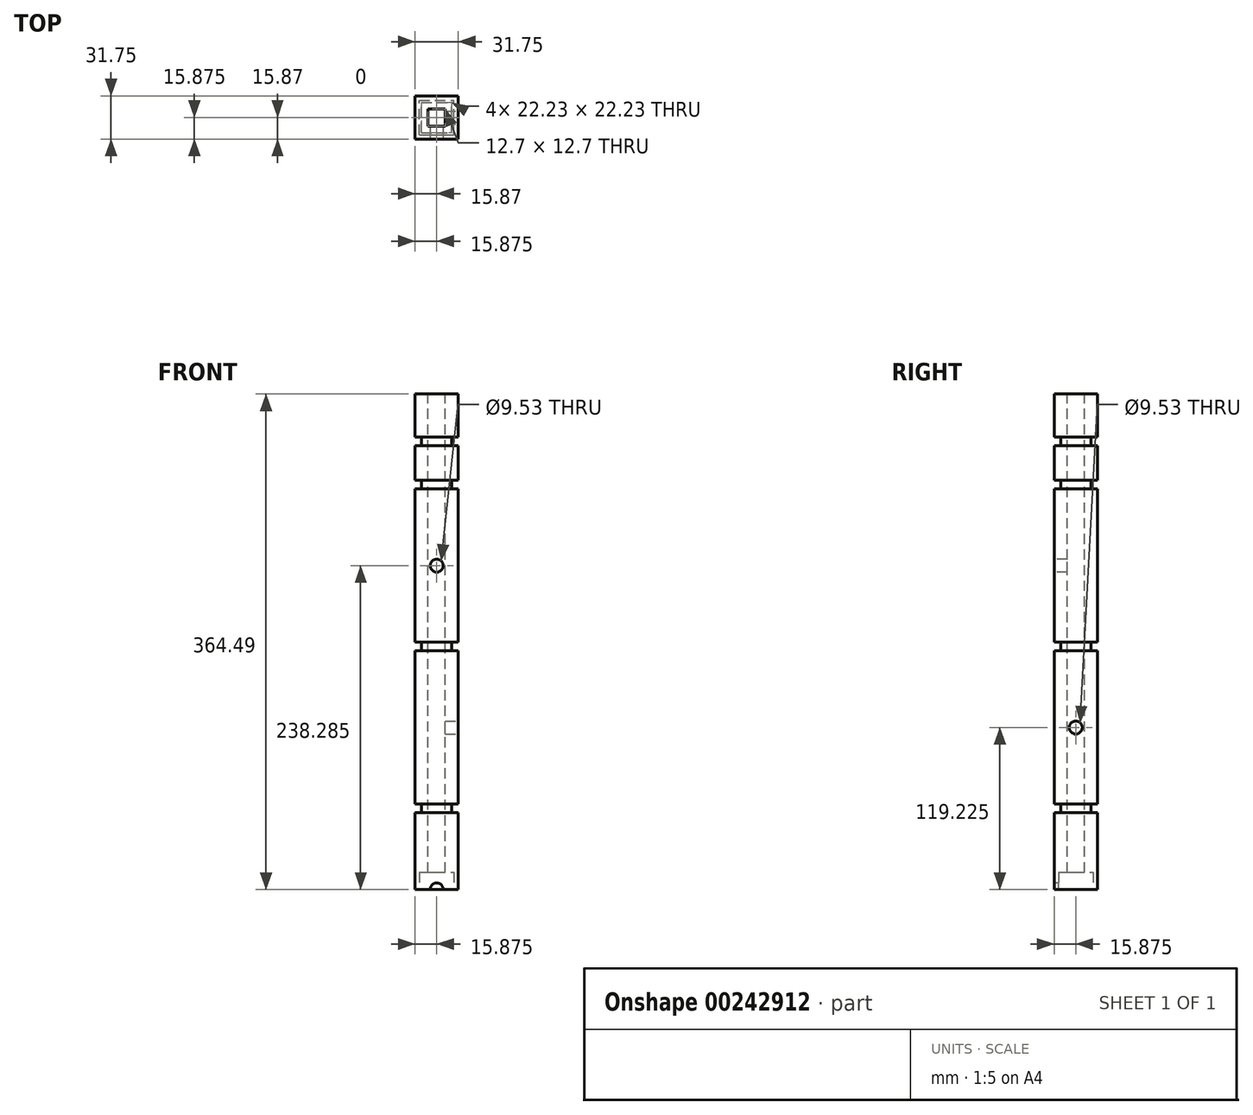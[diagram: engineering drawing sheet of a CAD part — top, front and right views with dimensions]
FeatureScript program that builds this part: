
annotation { "Feature Type Name" : "Feature", "Feature Type Description" : "" }
export const myFeature = defineFeature(function(context is Context, id is Id, definition is map)
    precondition{}
    {
        {
            var Q0;
            Q0=qCreatedBy(makeId("Top.planeOp"),FACE);
            var sketch = newSketch(context, id + "F0", { "sketchPlane" : qUnion([Q0])});
            skLineSegment(sketch, "E0", {"start": v(0, 0) * mm, "end": v(0, 31.75) * mm});
            skLineSegment(sketch, "E1", {"start": v(0, 31.75) * mm, "end": v(31.75, 31.75) * mm});
            skLineSegment(sketch, "E2", {"start": v(31.75, 31.75) * mm, "end": v(31.75, 0) * mm});
            skLineSegment(sketch, "E3", {"start": v(31.75, 0) * mm, "end": v(0, 0) * mm});
            skSolve(sketch);
        }
        {
            var Q0;
            Q0=makeQuery(id+"F0.imprint","IMPRINT",FACE,{"disambiguationData":[TD([[makeQuery(id+"F0.imprint","IMPRINT",EDGE,{"derivedFrom":sQuery(id+"F0.wireOp",EDGE,"E0")}),-1.0]])]});
            extrude(context, id + "F1", {"entities" : qUnion([Q0]), "depth" : 60.33 * mm});
        }
        {
            var Q0;
            Q0=makeQuery(id+"F1.opExtrude","CAP_FACE",FACE,{"disambiguationData":[OSD([sQuery(id+"F0.wireOp",EDGE,"E0"),sQuery(id+"F0.wireOp",EDGE,"E1"),sQuery(id+"F0.wireOp",EDGE,"E2"),sQuery(id+"F0.wireOp",EDGE,"E3")])],"isStart":false});
            var sketch = newSketch(context, id + "F2", { "sketchPlane" : qUnion([Q0])});
            skLineSegment(sketch, "E4", {"start": v(4.76, 4.76) * mm, "end": v(4.76, 26.99) * mm});
            skLineSegment(sketch, "E5", {"start": v(4.76, 26.99) * mm, "end": v(26.99, 26.99) * mm});
            skLineSegment(sketch, "E6", {"start": v(26.99, 26.99) * mm, "end": v(26.99, 4.76) * mm});
            skLineSegment(sketch, "E7", {"start": v(26.99, 4.76) * mm, "end": v(4.76, 4.76) * mm});
            skSolve(sketch);
        }
        {
            var Q0;
            Q0=makeQuery(id+"F2.imprint","IMPRINT",FACE,{"disambiguationData":[TD([[makeQuery(id+"F2.imprint","IMPRINT",EDGE,{"derivedFrom":sQuery(id+"F2.wireOp",EDGE,"E4")}),-1.0]])]});
            extrude(context, id + "F3", {"entities" : qUnion([Q0]), "operationType" : NewBodyOperationType.ADD, "depth" : 6.35 * mm});
        }
        {
            var Q0;
            Q0=makeQuery(id+"F3.opExtrude","CAP_FACE",FACE,{"disambiguationData":[OSD([sQuery(id+"F2.wireOp",EDGE,"E4"),sQuery(id+"F2.wireOp",EDGE,"E5"),sQuery(id+"F2.wireOp",EDGE,"E6"),sQuery(id+"F2.wireOp",EDGE,"E7")])],"isStart":false});
            var sketch = newSketch(context, id + "F4", { "sketchPlane" : qUnion([Q0])});
            skLineSegment(sketch, "E8.bottom", {"start": v(0, 0) * mm, "end": v(31.75, 0) * mm});
            skLineSegment(sketch, "E8.top", {"start": v(0, 31.75) * mm, "end": v(31.75, 31.75) * mm});
            skLineSegment(sketch, "E8.left", {"start": v(0, 0) * mm, "end": v(0, 31.75) * mm});
            skLineSegment(sketch, "E8.right", {"start": v(31.75, 0) * mm, "end": v(31.75, 31.75) * mm});
            skSolve(sketch);
        }
        {
            var Q0;
            Q0=qSketchRegion(id+"F4",true);
            extrude(context, id + "F5", {"entities" : qUnion([Q0]), "operationType" : NewBodyOperationType.ADD, "depth" : 112.7 * mm});
        }
        {
            var Q0;
            Q0=makeQuery(id+"F5.opExtrude","CAP_FACE",FACE,{"disambiguationData":[OSD([sQuery(id+"F4.wireOp",EDGE,"E8.bottom"),sQuery(id+"F4.wireOp",EDGE,"E8.top"),sQuery(id+"F4.wireOp",EDGE,"E8.left"),sQuery(id+"F4.wireOp",EDGE,"E8.right")])],"isStart":false});
            var sketch = newSketch(context, id + "F6", { "sketchPlane" : qUnion([Q0])});
            skLineSegment(sketch, "E9.bottom", {"start": v(0, 0) * mm, "end": v(4.76, 0) * mm});
            skLineSegment(sketch, "E9.top", {"start": v(0, 4.76) * mm, "end": v(4.76, 4.76) * mm});
            skLineSegment(sketch, "E9.left", {"start": v(0, 0) * mm, "end": v(0, 4.76) * mm});
            skLineSegment(sketch, "E9.right", {"start": v(4.76, 0) * mm, "end": v(4.76, 4.76) * mm});
            skLineSegment(sketch, "E10.bottom", {"start": v(4.76, 4.76) * mm, "end": v(26.99, 4.76) * mm});
            skLineSegment(sketch, "E10.top", {"start": v(4.76, 26.99) * mm, "end": v(26.99, 26.99) * mm});
            skLineSegment(sketch, "E10.left", {"start": v(4.76, 4.76) * mm, "end": v(4.76, 26.99) * mm});
            skLineSegment(sketch, "E10.right", {"start": v(26.99, 4.76) * mm, "end": v(26.99, 26.99) * mm});
            skSolve(sketch);
        }
        {
            var Q0;
            Q0=makeQuery(id+"F6.imprint","IMPRINT",FACE,{"disambiguationData":[TD([[makeQuery(id+"F6.imprint","IMPRINT",EDGE,{"derivedFrom":sQuery(id+"F6.wireOp",EDGE,"E10.bottom")}),1.0]])]});
            extrude(context, id + "F7", {"entities" : qUnion([Q0]), "operationType" : NewBodyOperationType.ADD, "depth" : 6.35 * mm});
        }
        {
            var Q0;
            Q0=makeQuery(id+"F7.opExtrude","CAP_FACE",FACE,{"disambiguationData":[OSD([sQuery(id+"F6.wireOp",EDGE,"E10.bottom"),sQuery(id+"F6.wireOp",EDGE,"E10.top"),sQuery(id+"F6.wireOp",EDGE,"E10.left"),sQuery(id+"F6.wireOp",EDGE,"E10.right")])],"isStart":false});
            var sketch = newSketch(context, id + "F8", { "sketchPlane" : qUnion([Q0])});
            skLineSegment(sketch, "E11.bottom", {"start": v(0, 0) * mm, "end": v(31.75, 0) * mm});
            skLineSegment(sketch, "E11.top", {"start": v(0, 31.75) * mm, "end": v(31.75, 31.75) * mm});
            skLineSegment(sketch, "E11.left", {"start": v(0, 0) * mm, "end": v(0, 31.75) * mm});
            skLineSegment(sketch, "E11.right", {"start": v(31.75, 0) * mm, "end": v(31.75, 31.75) * mm});
            skSolve(sketch);
        }
        {
            var Q0;
            Q0=makeQuery(id+"F8.imprint","IMPRINT",FACE,{"disambiguationData":[TD([[makeQuery(id+"F8.imprint","IMPRINT",EDGE,{"derivedFrom":sQuery(id+"F8.wireOp",EDGE,"E11.bottom")}),1.0]])]});
            var Q1;
            Q1=makeQuery(id+"F8.imprint","IMPRINT",FACE,{"disambiguationData":[TD([[makeQuery(id+"F8.imprint","IMPRINT",EDGE,{"derivedFrom":makeQuery(id+"F7.opExtrude","CAP_EDGE",EDGE,{"disambiguationData":[OSD([sQuery(id+"F6.wireOp",EDGE,"E10.bottom")])],"isStart":false})}),1.0]])]});
            extrude(context, id + "F9", {"entities" : qUnion([Q0, Q1]), "operationType" : NewBodyOperationType.ADD, "depth" : 112.7 * mm});
        }
        {
            var Q0;
            Q0=makeQuery(id+"F9.opExtrude","CAP_FACE",FACE,{"disambiguationData":[OSD([sQuery(id+"F8.wireOp",EDGE,"E11.bottom"),sQuery(id+"F8.wireOp",EDGE,"E11.top"),sQuery(id+"F8.wireOp",EDGE,"E11.left"),sQuery(id+"F8.wireOp",EDGE,"E11.right")])],"isStart":false});
            var sketch = newSketch(context, id + "F10", { "sketchPlane" : qUnion([Q0])});
            skLineSegment(sketch, "E12.bottom", {"start": v(0, 0) * mm, "end": v(4.76, 0) * mm});
            skLineSegment(sketch, "E12.top", {"start": v(0, 4.76) * mm, "end": v(4.76, 4.76) * mm});
            skLineSegment(sketch, "E12.left", {"start": v(0, 0) * mm, "end": v(0, 4.76) * mm});
            skLineSegment(sketch, "E12.right", {"start": v(4.76, 0) * mm, "end": v(4.76, 4.76) * mm});
            skLineSegment(sketch, "E13.bottom", {"start": v(4.76, 4.76) * mm, "end": v(27, 4.76) * mm});
            skLineSegment(sketch, "E13.top", {"start": v(4.76, 26.99) * mm, "end": v(26.99, 26.99) * mm});
            skLineSegment(sketch, "E13.left", {"start": v(4.76, 4.76) * mm, "end": v(4.76, 26.99) * mm});
            skLineSegment(sketch, "E13.right", {"start": v(27, 4.76) * mm, "end": v(26.99, 26.99) * mm});
            skLineSegment(sketch, "E14.bottom", {"start": v(26.99, 26.99) * mm, "end": v(31.75, 26.99) * mm});
            skLineSegment(sketch, "E14.top", {"start": v(26.99, 31.75) * mm, "end": v(31.75, 31.75) * mm});
            skLineSegment(sketch, "E14.left", {"start": v(26.99, 26.99) * mm, "end": v(26.99, 31.75) * mm});
            skLineSegment(sketch, "E14.right", {"start": v(31.75, 26.99) * mm, "end": v(31.75, 31.75) * mm});
            skSolve(sketch);
        }
        {
            var Q0;
            Q0=makeQuery(id+"F10.imprint","IMPRINT",FACE,{"disambiguationData":[TD([[makeQuery(id+"F10.imprint","IMPRINT",EDGE,{"derivedFrom":sQuery(id+"F10.wireOp",EDGE,"E13.bottom")}),1.0]])]});
            extrude(context, id + "F11", {"entities" : qUnion([Q0]), "operationType" : NewBodyOperationType.ADD, "depth" : 6.35 * mm});
        }
        {
            var Q0;
            Q0=makeQuery(id+"F11.opExtrude","CAP_FACE",FACE,{"disambiguationData":[OSD([sQuery(id+"F10.wireOp",EDGE,"E13.bottom"),sQuery(id+"F10.wireOp",EDGE,"E13.top"),sQuery(id+"F10.wireOp",EDGE,"E13.left"),sQuery(id+"F10.wireOp",EDGE,"E13.right")])],"isStart":false});
            var sketch = newSketch(context, id + "F12", { "sketchPlane" : qUnion([Q0])});
            skLineSegment(sketch, "E15.bottom", {"start": v(0, 0) * mm, "end": v(31.75, 0) * mm});
            skLineSegment(sketch, "E15.top", {"start": v(0, 31.75) * mm, "end": v(31.75, 31.75) * mm});
            skLineSegment(sketch, "E15.left", {"start": v(0, 0) * mm, "end": v(0, 31.75) * mm});
            skLineSegment(sketch, "E15.right", {"start": v(31.75, 0) * mm, "end": v(31.75, 31.75) * mm});
            skSolve(sketch);
        }
        {
            var Q0;
            Q0=makeQuery(id+"F12.imprint","IMPRINT",FACE,{"disambiguationData":[TD([[makeQuery(id+"F12.imprint","IMPRINT",EDGE,{"derivedFrom":makeQuery(id+"F11.opExtrude","CAP_EDGE",EDGE,{"disambiguationData":[OSD([sQuery(id+"F10.wireOp",EDGE,"E13.bottom")])],"isStart":false})}),1.0]])]});
            var Q1;
            Q1=makeQuery(id+"F12.imprint","IMPRINT",FACE,{"disambiguationData":[TD([[makeQuery(id+"F12.imprint","IMPRINT",EDGE,{"derivedFrom":sQuery(id+"F12.wireOp",EDGE,"E15.bottom")}),1.0]])]});
            extrude(context, id + "F13", {"entities" : qUnion([Q0, Q1]), "operationType" : NewBodyOperationType.ADD, "depth" : 112.7 * mm});
        }
        {
            var Q0;
            Q0=makeQuery(id+"F13.opExtrude","CAP_FACE",FACE,{"disambiguationData":[OSD([sQuery(id+"F12.wireOp",EDGE,"E15.bottom"),sQuery(id+"F12.wireOp",EDGE,"E15.top"),sQuery(id+"F12.wireOp",EDGE,"E15.left"),sQuery(id+"F12.wireOp",EDGE,"E15.right")])],"isStart":false});
            var sketch = newSketch(context, id + "F14", { "sketchPlane" : qUnion([Q0])});
            skLineSegment(sketch, "E16.bottom", {"start": v(0, 0) * mm, "end": v(4.76, 0) * mm});
            skLineSegment(sketch, "E16.top", {"start": v(0, 4.76) * mm, "end": v(4.76, 4.76) * mm});
            skLineSegment(sketch, "E16.left", {"start": v(0, 0) * mm, "end": v(0, 4.76) * mm});
            skLineSegment(sketch, "E16.right", {"start": v(4.76, 0) * mm, "end": v(4.76, 4.76) * mm});
            skLineSegment(sketch, "E17.bottom", {"start": v(4.76, 4.76) * mm, "end": v(27, 4.76) * mm});
            skLineSegment(sketch, "E17.top", {"start": v(4.76, 26.99) * mm, "end": v(26.99, 26.99) * mm});
            skLineSegment(sketch, "E17.left", {"start": v(4.76, 4.76) * mm, "end": v(4.76, 26.99) * mm});
            skLineSegment(sketch, "E17.right", {"start": v(27, 4.76) * mm, "end": v(26.99, 26.99) * mm});
            skLineSegment(sketch, "E18.bottom", {"start": v(26.99, 26.99) * mm, "end": v(31.75, 26.99) * mm});
            skLineSegment(sketch, "E18.top", {"start": v(26.99, 31.75) * mm, "end": v(31.75, 31.75) * mm});
            skLineSegment(sketch, "E18.left", {"start": v(26.99, 26.99) * mm, "end": v(26.99, 31.75) * mm});
            skLineSegment(sketch, "E18.right", {"start": v(31.75, 26.99) * mm, "end": v(31.75, 31.75) * mm});
            skSolve(sketch);
        }
        {
            var Q0;
            Q0=makeQuery(id+"F14.imprint","IMPRINT",FACE,{"disambiguationData":[TD([[makeQuery(id+"F14.imprint","IMPRINT",EDGE,{"derivedFrom":sQuery(id+"F14.wireOp",EDGE,"E17.bottom")}),1.0]])]});
            extrude(context, id + "F15", {"entities" : qUnion([Q0]), "operationType" : NewBodyOperationType.ADD, "depth" : 6.35 * mm});
        }
        {
            var Q0;
            Q0=makeQuery(id+"F15.opExtrude","CAP_FACE",FACE,{"disambiguationData":[OSD([sQuery(id+"F14.wireOp",EDGE,"E17.bottom"),sQuery(id+"F14.wireOp",EDGE,"E17.top"),sQuery(id+"F14.wireOp",EDGE,"E17.left"),sQuery(id+"F14.wireOp",EDGE,"E17.right")])],"isStart":false});
            var sketch = newSketch(context, id + "F16", { "sketchPlane" : qUnion([Q0])});
            skLineSegment(sketch, "E19.bottom", {"start": v(0, 0) * mm, "end": v(31.75, 0) * mm});
            skLineSegment(sketch, "E19.top", {"start": v(0, 31.75) * mm, "end": v(31.75, 31.75) * mm});
            skLineSegment(sketch, "E19.left", {"start": v(0, 0) * mm, "end": v(0, 31.75) * mm});
            skLineSegment(sketch, "E19.right", {"start": v(31.75, 0) * mm, "end": v(31.75, 31.75) * mm});
            skSolve(sketch);
        }
        {
            var Q0;
            Q0=qSketchRegion(id+"F16",true);
            extrude(context, id + "F17", {"entities" : qUnion([Q0]), "operationType" : NewBodyOperationType.ADD, "depth" : 112.7 * mm});
        }
        {
            var Q0;
            Q0=makeQuery(id+"F17.opExtrude","CAP_FACE",FACE,{"disambiguationData":[OSD([sQuery(id+"F16.wireOp",EDGE,"E19.bottom"),sQuery(id+"F16.wireOp",EDGE,"E19.top"),sQuery(id+"F16.wireOp",EDGE,"E19.left"),sQuery(id+"F16.wireOp",EDGE,"E19.right")])],"isStart":false});
            var sketch = newSketch(context, id + "F18", { "sketchPlane" : qUnion([Q0])});
            skLineSegment(sketch, "E20.bottom", {"start": v(0, 0) * mm, "end": v(4.76, 0) * mm});
            skLineSegment(sketch, "E20.top", {"start": v(0, 4.76) * mm, "end": v(4.76, 4.76) * mm});
            skLineSegment(sketch, "E20.left", {"start": v(0, 0) * mm, "end": v(0, 4.76) * mm});
            skLineSegment(sketch, "E20.right", {"start": v(4.76, 0) * mm, "end": v(4.76, 4.76) * mm});
            skLineSegment(sketch, "E21.bottom", {"start": v(4.76, 4.76) * mm, "end": v(27, 4.76) * mm});
            skLineSegment(sketch, "E21.top", {"start": v(4.76, 26.99) * mm, "end": v(26.99, 26.99) * mm});
            skLineSegment(sketch, "E21.left", {"start": v(4.76, 4.76) * mm, "end": v(4.76, 26.99) * mm});
            skLineSegment(sketch, "E21.right", {"start": v(27, 4.76) * mm, "end": v(26.99, 26.99) * mm});
            skLineSegment(sketch, "E22.bottom", {"start": v(26.99, 26.99) * mm, "end": v(31.75, 26.99) * mm});
            skLineSegment(sketch, "E22.top", {"start": v(26.99, 31.75) * mm, "end": v(31.75, 31.75) * mm});
            skLineSegment(sketch, "E22.left", {"start": v(26.99, 26.99) * mm, "end": v(26.99, 31.75) * mm});
            skLineSegment(sketch, "E22.right", {"start": v(31.75, 26.99) * mm, "end": v(31.75, 31.75) * mm});
            skSolve(sketch);
        }
        {
            var Q0;
            Q0=makeQuery(id+"F18.imprint","IMPRINT",FACE,{"disambiguationData":[TD([[makeQuery(id+"F18.imprint","IMPRINT",EDGE,{"derivedFrom":sQuery(id+"F18.wireOp",EDGE,"E21.bottom")}),1.0]])]});
            extrude(context, id + "F19", {"entities" : qUnion([Q0]), "operationType" : NewBodyOperationType.ADD, "depth" : 6.35 * mm});
        }
        {
            var Q0;
            Q0=makeQuery(id+"F19.opExtrude","CAP_FACE",FACE,{"disambiguationData":[OSD([sQuery(id+"F18.wireOp",EDGE,"E21.bottom"),sQuery(id+"F18.wireOp",EDGE,"E21.top"),sQuery(id+"F18.wireOp",EDGE,"E21.left"),sQuery(id+"F18.wireOp",EDGE,"E21.right")])],"isStart":false});
            var sketch = newSketch(context, id + "F20", { "sketchPlane" : qUnion([Q0])});
            skLineSegment(sketch, "E23.bottom", {"start": v(0, 0) * mm, "end": v(31.75, 0) * mm});
            skLineSegment(sketch, "E23.top", {"start": v(0, 31.75) * mm, "end": v(31.75, 31.75) * mm});
            skLineSegment(sketch, "E23.left", {"start": v(0, 0) * mm, "end": v(0, 31.75) * mm});
            skLineSegment(sketch, "E23.right", {"start": v(31.75, 0) * mm, "end": v(31.75, 31.75) * mm});
            skSolve(sketch);
        }
        {
            var Q0;
            Q0=makeQuery(id+"F20.imprint","IMPRINT",FACE,{"disambiguationData":[TD([[makeQuery(id+"F20.imprint","IMPRINT",EDGE,{"derivedFrom":sQuery(id+"F20.wireOp",EDGE,"E23.bottom")}),1.0]])]});
            var Q1;
            Q1=makeQuery(id+"F20.imprint","IMPRINT",FACE,{"disambiguationData":[TD([[makeQuery(id+"F20.imprint","IMPRINT",EDGE,{"derivedFrom":makeQuery(id+"F19.opExtrude","CAP_EDGE",EDGE,{"disambiguationData":[OSD([sQuery(id+"F18.wireOp",EDGE,"E21.bottom")])],"isStart":false})}),1.0]])]});
            extrude(context, id + "F21", {"entities" : qUnion([Q0, Q1]), "operationType" : NewBodyOperationType.ADD, "depth" : 112.7 * mm});
        }
        {
            var Q0;
            Q0=makeQuery(id+"F21.opExtrude","CAP_FACE",FACE,{"disambiguationData":[OSD([sQuery(id+"F20.wireOp",EDGE,"E23.bottom"),sQuery(id+"F20.wireOp",EDGE,"E23.top"),sQuery(id+"F20.wireOp",EDGE,"E23.left"),sQuery(id+"F20.wireOp",EDGE,"E23.right")])],"isStart":false});
            var sketch = newSketch(context, id + "F22", { "sketchPlane" : qUnion([Q0])});
            skLineSegment(sketch, "E24.bottom", {"start": v(0, 0) * mm, "end": v(4.76, 0) * mm});
            skLineSegment(sketch, "E24.top", {"start": v(0, 4.76) * mm, "end": v(4.76, 4.76) * mm});
            skLineSegment(sketch, "E24.left", {"start": v(0, 0) * mm, "end": v(0, 4.76) * mm});
            skLineSegment(sketch, "E24.right", {"start": v(4.76, 0) * mm, "end": v(4.76, 4.76) * mm});
            skLineSegment(sketch, "E25.bottom", {"start": v(4.76, 4.76) * mm, "end": v(27, 4.76) * mm});
            skLineSegment(sketch, "E25.top", {"start": v(4.76, 26.99) * mm, "end": v(26.99, 26.99) * mm});
            skLineSegment(sketch, "E25.left", {"start": v(4.76, 4.76) * mm, "end": v(4.76, 26.99) * mm});
            skLineSegment(sketch, "E25.right", {"start": v(27, 4.76) * mm, "end": v(26.99, 26.99) * mm});
            skLineSegment(sketch, "E26.bottom", {"start": v(26.99, 26.99) * mm, "end": v(31.75, 26.99) * mm});
            skLineSegment(sketch, "E26.top", {"start": v(26.99, 31.75) * mm, "end": v(31.75, 31.75) * mm});
            skLineSegment(sketch, "E26.left", {"start": v(26.99, 26.99) * mm, "end": v(26.99, 31.75) * mm});
            skLineSegment(sketch, "E26.right", {"start": v(31.75, 26.99) * mm, "end": v(31.75, 31.75) * mm});
            skSolve(sketch);
        }
        {
            var Q0;
            Q0=makeQuery(id+"F22.imprint","IMPRINT",FACE,{"disambiguationData":[TD([[makeQuery(id+"F22.imprint","IMPRINT",EDGE,{"derivedFrom":sQuery(id+"F22.wireOp",EDGE,"E25.bottom")}),1.0]])]});
            extrude(context, id + "F23", {"entities" : qUnion([Q0]), "operationType" : NewBodyOperationType.ADD, "depth" : 6.35 * mm});
        }
        {
            var Q0;
            Q0=makeQuery(id+"F23.opExtrude","CAP_FACE",FACE,{"disambiguationData":[OSD([sQuery(id+"F22.wireOp",EDGE,"E25.bottom"),sQuery(id+"F22.wireOp",EDGE,"E25.top"),sQuery(id+"F22.wireOp",EDGE,"E25.left"),sQuery(id+"F22.wireOp",EDGE,"E25.right")])],"isStart":false});
            var sketch = newSketch(context, id + "F24", { "sketchPlane" : qUnion([Q0])});
            skLineSegment(sketch, "E27.bottom", {"start": v(0, 0) * mm, "end": v(31.75, 0) * mm});
            skLineSegment(sketch, "E27.top", {"start": v(0, 31.75) * mm, "end": v(31.75, 31.75) * mm});
            skLineSegment(sketch, "E27.left", {"start": v(0, 0) * mm, "end": v(0, 31.75) * mm});
            skLineSegment(sketch, "E27.right", {"start": v(31.75, 0) * mm, "end": v(31.75, 31.75) * mm});
            skSolve(sketch);
        }
        {
            var Q0;
            Q0=makeQuery(id+"F24.imprint","IMPRINT",FACE,{"disambiguationData":[TD([[makeQuery(id+"F24.imprint","IMPRINT",EDGE,{"derivedFrom":sQuery(id+"F24.wireOp",EDGE,"E27.bottom")}),1.0]])]});
            var Q1;
            Q1=makeQuery(id+"F24.imprint","IMPRINT",FACE,{"disambiguationData":[TD([[makeQuery(id+"F24.imprint","IMPRINT",EDGE,{"derivedFrom":makeQuery(id+"F23.opExtrude","CAP_EDGE",EDGE,{"disambiguationData":[OSD([sQuery(id+"F22.wireOp",EDGE,"E25.bottom")])],"isStart":false})}),1.0]])]});
            extrude(context, id + "F25", {"entities" : qUnion([Q0, Q1]), "operationType" : NewBodyOperationType.ADD, "depth" : 25.4 * mm});
        }
        {
            var Q0;
            Q0=makeQuery(id+"F25.opExtrude","CAP_FACE",FACE,{"disambiguationData":[OSD([sQuery(id+"F24.wireOp",EDGE,"E27.bottom"),sQuery(id+"F24.wireOp",EDGE,"E27.top"),sQuery(id+"F24.wireOp",EDGE,"E27.left"),sQuery(id+"F24.wireOp",EDGE,"E27.right")])],"isStart":false});
            var sketch = newSketch(context, id + "F26", { "sketchPlane" : qUnion([Q0])});
            skLineSegment(sketch, "E28.bottom", {"start": v(0, 0) * mm, "end": v(4.76, 0) * mm});
            skLineSegment(sketch, "E28.top", {"start": v(0, 4.76) * mm, "end": v(4.76, 4.76) * mm});
            skLineSegment(sketch, "E28.left", {"start": v(0, 0) * mm, "end": v(0, 4.76) * mm});
            skLineSegment(sketch, "E28.right", {"start": v(4.76, 0) * mm, "end": v(4.76, 4.76) * mm});
            skLineSegment(sketch, "E29.bottom", {"start": v(4.76, 4.76) * mm, "end": v(27, 4.76) * mm});
            skLineSegment(sketch, "E29.top", {"start": v(4.76, 26.99) * mm, "end": v(26.99, 26.99) * mm});
            skLineSegment(sketch, "E29.left", {"start": v(4.76, 4.76) * mm, "end": v(4.76, 26.99) * mm});
            skLineSegment(sketch, "E29.right", {"start": v(27, 4.76) * mm, "end": v(26.99, 26.99) * mm});
            skLineSegment(sketch, "E30.bottom", {"start": v(26.99, 26.99) * mm, "end": v(31.75, 26.99) * mm});
            skLineSegment(sketch, "E30.top", {"start": v(26.99, 31.75) * mm, "end": v(31.75, 31.75) * mm});
            skLineSegment(sketch, "E30.left", {"start": v(26.99, 26.99) * mm, "end": v(26.99, 31.75) * mm});
            skLineSegment(sketch, "E30.right", {"start": v(31.75, 26.99) * mm, "end": v(31.75, 31.75) * mm});
            skSolve(sketch);
        }
        {
            var Q0;
            Q0=makeQuery(id+"F26.imprint","IMPRINT",FACE,{"disambiguationData":[TD([[makeQuery(id+"F26.imprint","IMPRINT",EDGE,{"derivedFrom":sQuery(id+"F26.wireOp",EDGE,"E29.bottom")}),1.0]])]});
            extrude(context, id + "F27", {"entities" : qUnion([Q0]), "operationType" : NewBodyOperationType.ADD, "depth" : 6.35 * mm});
        }
        {
            var Q0;
            Q0=makeQuery(id+"F27.opExtrude","CAP_FACE",FACE,{"disambiguationData":[OSD([sQuery(id+"F26.wireOp",EDGE,"E29.bottom"),sQuery(id+"F26.wireOp",EDGE,"E29.top"),sQuery(id+"F26.wireOp",EDGE,"E29.left"),sQuery(id+"F26.wireOp",EDGE,"E29.right")])],"isStart":false});
            var sketch = newSketch(context, id + "F28", { "sketchPlane" : qUnion([Q0])});
            skLineSegment(sketch, "E31.bottom", {"start": v(0, 0) * mm, "end": v(31.75, 0) * mm});
            skLineSegment(sketch, "E31.top", {"start": v(0, 31.75) * mm, "end": v(31.75, 31.75) * mm});
            skLineSegment(sketch, "E31.left", {"start": v(0, 0) * mm, "end": v(0, 31.75) * mm});
            skLineSegment(sketch, "E31.right", {"start": v(31.75, 0) * mm, "end": v(31.75, 31.75) * mm});
            skSolve(sketch);
        }
        {
            var Q0;
            Q0=makeQuery(id+"F28.imprint","IMPRINT",FACE,{"disambiguationData":[TD([[makeQuery(id+"F28.imprint","IMPRINT",EDGE,{"derivedFrom":sQuery(id+"F28.wireOp",EDGE,"E31.bottom")}),1.0]])]});
            var Q1;
            Q1=makeQuery(id+"F28.imprint","IMPRINT",FACE,{"disambiguationData":[TD([[makeQuery(id+"F28.imprint","IMPRINT",EDGE,{"derivedFrom":makeQuery(id+"F27.opExtrude","CAP_EDGE",EDGE,{"disambiguationData":[OSD([sQuery(id+"F26.wireOp",EDGE,"E29.bottom")])],"isStart":false})}),1.0]])]});
            extrude(context, id + "F29", {"entities" : qUnion([Q0, Q1]), "operationType" : NewBodyOperationType.ADD, "depth" : 31.75 * mm});
        }
        {
            var Q0;
            Q0=makeQuery(id+"F1.opExtrude","CAP_FACE",FACE,{"disambiguationData":[OSD([sQuery(id+"F0.wireOp",EDGE,"E0"),sQuery(id+"F0.wireOp",EDGE,"E1"),sQuery(id+"F0.wireOp",EDGE,"E2"),sQuery(id+"F0.wireOp",EDGE,"E3")])],"isStart":true});
            var sketch = newSketch(context, id + "F30", { "sketchPlane" : qUnion([Q0])});
            skLineSegment(sketch, "E32.bottom", {"start": v(0, -31.75) * mm, "end": v(15.88, -31.75) * mm});
            skLineSegment(sketch, "E32.top", {"start": v(0, -15.87) * mm, "end": v(15.88, -15.87) * mm});
            skLineSegment(sketch, "E32.left", {"start": v(0, -31.75) * mm, "end": v(0, -15.87) * mm});
            skLineSegment(sketch, "E32.right", {"start": v(15.88, -31.75) * mm, "end": v(15.88, -15.87) * mm});
            skLineSegment(sketch, "E33", {"start": v(0, -31.75) * mm, "end": v(31.75, -31.75) * mm});
            skCircle(sketch, "E34", {"center": v(15.88, -15.87) * mm, "radius": 15.88 * mm});
            skCircle(sketch, "E35", {"center": v(15.88, -15.87) * mm, "radius": 9.53 * mm});
            skSolve(sketch);
        }
        {
            var Q0;
            Q0=makeQuery(id+"F5.opExtrude","SWEPT_FACE",FACE,{"disambiguationData":[OSD([sQuery(id+"F4.wireOp",EDGE,"E8.bottom")])]});
            var sketch = newSketch(context, id + "F31", { "sketchPlane" : qUnion([Q0])});
            skLineSegment(sketch, "E36.bottom", {"start": v(31.75, 123.04) * mm, "end": v(15.88, 123.04) * mm});
            skLineSegment(sketch, "E36.top", {"start": v(31.75, 66.68) * mm, "end": v(15.88, 66.68) * mm});
            skLineSegment(sketch, "E36.left", {"start": v(31.75, 123.04) * mm, "end": v(31.75, 66.68) * mm});
            skLineSegment(sketch, "E36.right", {"start": v(15.88, 123.04) * mm, "end": v(15.88, 66.68) * mm});
            skCircle(sketch, "E37", {"center": v(15.88, 123.04) * mm, "radius": 4.77 * mm});
            skSolve(sketch);
        }
        {
            var Q0;
            {var subQ0=sQuery(id+"F31.wireOp",EDGE,"E36.right");var subQ1=sQuery(id+"F31.wireOp",EDGE,"E36.bottom");var subQ2=makeQuery(id+"F31.imprint","INTERSECT",VERTEX,{"derivedFrom":[subQ1,subQ0]});Q0=makeQuery(id+"F31.imprint","IMPRINT",FACE,{"disambiguationData":[TD([[makeQuery(id+"F31.imprint","IMPRINT",EDGE,{"disambiguationData":[TD([[subQ2,1.0]])],"derivedFrom":subQ1}),-1.0]])]});}
            var Q1;
            {var subQ0=sQuery(id+"F31.wireOp",EDGE,"E36.right");var subQ1=sQuery(id+"F31.wireOp",EDGE,"E36.bottom");var subQ2=makeQuery(id+"F31.imprint","INTERSECT",VERTEX,{"derivedFrom":[subQ1,subQ0]});Q1=makeQuery(id+"F31.imprint","IMPRINT",FACE,{"disambiguationData":[TD([[makeQuery(id+"F31.imprint","IMPRINT",EDGE,{"disambiguationData":[TD([[subQ2,1.0]])],"derivedFrom":subQ1}),1.0]])]});}
            extrude(context, id + "F32", {"entities" : qUnion([Q0, Q1]), "operationType" : NewBodyOperationType.REMOVE, "oppositeDirection" : true, "depth" : 12.7 * mm});
        }
        {
            var Q0;
            Q0=makeQuery(id+"F9.opExtrude","SWEPT_FACE",FACE,{"disambiguationData":[OSD([sQuery(id+"F8.wireOp",EDGE,"E11.right")])]});
            var sketch = newSketch(context, id + "F33", { "sketchPlane" : qUnion([Q0])});
            skLineSegment(sketch, "E38.bottom", {"start": v(31.75, 242.1) * mm, "end": v(15.88, 242.1) * mm});
            skLineSegment(sketch, "E38.top", {"start": v(31.75, 185.74) * mm, "end": v(15.88, 185.74) * mm});
            skLineSegment(sketch, "E38.left", {"start": v(31.75, 242.1) * mm, "end": v(31.75, 185.74) * mm});
            skLineSegment(sketch, "E38.right", {"start": v(15.88, 242.1) * mm, "end": v(15.88, 185.74) * mm});
            skCircle(sketch, "E39", {"center": v(15.88, 242.1) * mm, "radius": 4.77 * mm});
            skSolve(sketch);
        }
        {
            var Q0;
            {var subQ0=sQuery(id+"F33.wireOp",EDGE,"E38.right");var subQ1=sQuery(id+"F33.wireOp",EDGE,"E38.bottom");var subQ2=makeQuery(id+"F33.imprint","INTERSECT",VERTEX,{"derivedFrom":[subQ1,subQ0]});Q0=makeQuery(id+"F33.imprint","IMPRINT",FACE,{"disambiguationData":[TD([[makeQuery(id+"F33.imprint","IMPRINT",EDGE,{"disambiguationData":[TD([[subQ2,1.0]])],"derivedFrom":subQ1}),-1.0]])]});}
            var Q1;
            {var subQ0=sQuery(id+"F33.wireOp",EDGE,"E38.right");var subQ1=sQuery(id+"F33.wireOp",EDGE,"E38.bottom");var subQ2=makeQuery(id+"F33.imprint","INTERSECT",VERTEX,{"derivedFrom":[subQ1,subQ0]});Q1=makeQuery(id+"F33.imprint","IMPRINT",FACE,{"disambiguationData":[TD([[makeQuery(id+"F33.imprint","IMPRINT",EDGE,{"disambiguationData":[TD([[subQ2,1.0]])],"derivedFrom":subQ1}),1.0]])]});}
            extrude(context, id + "F34", {"entities" : qUnion([Q0, Q1]), "operationType" : NewBodyOperationType.REMOVE, "oppositeDirection" : true, "depth" : 12.7 * mm});
        }
        {
            var Q0;
            Q0=makeQuery(id+"F13.opExtrude","SWEPT_FACE",FACE,{"disambiguationData":[OSD([sQuery(id+"F12.wireOp",EDGE,"E15.bottom")])]});
            var sketch = newSketch(context, id + "F35", { "sketchPlane" : qUnion([Q0])});
            skLineSegment(sketch, "E40.bottom", {"start": v(31.75, 361.16) * mm, "end": v(15.88, 361.16) * mm});
            skLineSegment(sketch, "E40.top", {"start": v(31.75, 304.8) * mm, "end": v(15.88, 304.8) * mm});
            skLineSegment(sketch, "E40.left", {"start": v(31.75, 361.16) * mm, "end": v(31.75, 304.8) * mm});
            skLineSegment(sketch, "E40.right", {"start": v(15.88, 361.16) * mm, "end": v(15.88, 304.8) * mm});
            skCircle(sketch, "E41", {"center": v(15.88, 361.16) * mm, "radius": 4.77 * mm});
            skSolve(sketch);
        }
        {
            var Q0;
            {var subQ0=sQuery(id+"F35.wireOp",EDGE,"E40.right");var subQ1=sQuery(id+"F35.wireOp",EDGE,"E40.bottom");var subQ2=makeQuery(id+"F35.imprint","INTERSECT",VERTEX,{"derivedFrom":[subQ1,subQ0]});Q0=makeQuery(id+"F35.imprint","IMPRINT",FACE,{"disambiguationData":[TD([[makeQuery(id+"F35.imprint","IMPRINT",EDGE,{"disambiguationData":[TD([[subQ2,1.0]])],"derivedFrom":subQ1}),-1.0]])]});}
            var Q1;
            {var subQ0=sQuery(id+"F35.wireOp",EDGE,"E40.right");var subQ1=sQuery(id+"F35.wireOp",EDGE,"E40.bottom");var subQ2=makeQuery(id+"F35.imprint","INTERSECT",VERTEX,{"derivedFrom":[subQ1,subQ0]});Q1=makeQuery(id+"F35.imprint","IMPRINT",FACE,{"disambiguationData":[TD([[makeQuery(id+"F35.imprint","IMPRINT",EDGE,{"disambiguationData":[TD([[subQ2,1.0]])],"derivedFrom":subQ1}),1.0]])]});}
            extrude(context, id + "F36", {"entities" : qUnion([Q0, Q1]), "operationType" : NewBodyOperationType.REMOVE, "oppositeDirection" : true, "depth" : 12.7 * mm});
        }
        {
            var Q0;
            Q0=makeQuery(id+"F17.opExtrude","SWEPT_FACE",FACE,{"disambiguationData":[OSD([sQuery(id+"F16.wireOp",EDGE,"E19.right")])]});
            var sketch = newSketch(context, id + "F37", { "sketchPlane" : qUnion([Q0])});
            skLineSegment(sketch, "E42.bottom", {"start": v(31.75, 480.21) * mm, "end": v(15.88, 480.21) * mm});
            skLineSegment(sketch, "E42.top", {"start": v(31.75, 423.86) * mm, "end": v(15.88, 423.86) * mm});
            skLineSegment(sketch, "E42.left", {"start": v(31.75, 480.21) * mm, "end": v(31.75, 423.86) * mm});
            skLineSegment(sketch, "E42.right", {"start": v(15.88, 480.21) * mm, "end": v(15.88, 423.86) * mm});
            skCircle(sketch, "E43", {"center": v(15.88, 480.21) * mm, "radius": 4.77 * mm});
            skSolve(sketch);
        }
        {
            var Q0;
            {var subQ0=sQuery(id+"F37.wireOp",EDGE,"E42.right");var subQ1=sQuery(id+"F37.wireOp",EDGE,"E42.bottom");var subQ2=makeQuery(id+"F37.imprint","INTERSECT",VERTEX,{"derivedFrom":[subQ1,subQ0]});Q0=makeQuery(id+"F37.imprint","IMPRINT",FACE,{"disambiguationData":[TD([[makeQuery(id+"F37.imprint","IMPRINT",EDGE,{"disambiguationData":[TD([[subQ2,1.0]])],"derivedFrom":subQ1}),-1.0]])]});}
            var Q1;
            {var subQ0=sQuery(id+"F37.wireOp",EDGE,"E42.right");var subQ1=sQuery(id+"F37.wireOp",EDGE,"E42.bottom");var subQ2=makeQuery(id+"F37.imprint","INTERSECT",VERTEX,{"derivedFrom":[subQ1,subQ0]});Q1=makeQuery(id+"F37.imprint","IMPRINT",FACE,{"disambiguationData":[TD([[makeQuery(id+"F37.imprint","IMPRINT",EDGE,{"disambiguationData":[TD([[subQ2,1.0]])],"derivedFrom":subQ1}),1.0]])]});}
            extrude(context, id + "F38", {"entities" : qUnion([Q0, Q1]), "operationType" : NewBodyOperationType.REMOVE, "oppositeDirection" : true, "depth" : 12.7 * mm});
        }
        {
            var Q0;
            Q0=makeQuery(id+"F21.opExtrude","SWEPT_FACE",FACE,{"disambiguationData":[OSD([sQuery(id+"F20.wireOp",EDGE,"E23.bottom")])]});
            var sketch = newSketch(context, id + "F39", { "sketchPlane" : qUnion([Q0])});
            skLineSegment(sketch, "E44.bottom", {"start": v(31.75, 599.27) * mm, "end": v(15.88, 599.27) * mm});
            skLineSegment(sketch, "E44.top", {"start": v(31.75, 542.92) * mm, "end": v(15.88, 542.92) * mm});
            skLineSegment(sketch, "E44.left", {"start": v(31.75, 599.27) * mm, "end": v(31.75, 542.92) * mm});
            skLineSegment(sketch, "E44.right", {"start": v(15.88, 599.27) * mm, "end": v(15.88, 542.92) * mm});
            skCircle(sketch, "E45", {"center": v(15.88, 599.27) * mm, "radius": 4.77 * mm});
            skSolve(sketch);
        }
        {
            var Q0;
            {var subQ0=sQuery(id+"F39.wireOp",EDGE,"E44.right");var subQ1=sQuery(id+"F39.wireOp",EDGE,"E44.bottom");var subQ2=makeQuery(id+"F39.imprint","INTERSECT",VERTEX,{"derivedFrom":[subQ1,subQ0]});Q0=makeQuery(id+"F39.imprint","IMPRINT",FACE,{"disambiguationData":[TD([[makeQuery(id+"F39.imprint","IMPRINT",EDGE,{"disambiguationData":[TD([[subQ2,1.0]])],"derivedFrom":subQ1}),-1.0]])]});}
            var Q1;
            {var subQ0=sQuery(id+"F39.wireOp",EDGE,"E44.right");var subQ1=sQuery(id+"F39.wireOp",EDGE,"E44.bottom");var subQ2=makeQuery(id+"F39.imprint","INTERSECT",VERTEX,{"derivedFrom":[subQ1,subQ0]});Q1=makeQuery(id+"F39.imprint","IMPRINT",FACE,{"disambiguationData":[TD([[makeQuery(id+"F39.imprint","IMPRINT",EDGE,{"disambiguationData":[TD([[subQ2,1.0]])],"derivedFrom":subQ1}),1.0]])]});}
            extrude(context, id + "F40", {"entities" : qUnion([Q0, Q1]), "operationType" : NewBodyOperationType.REMOVE, "oppositeDirection" : true, "depth" : 12.7 * mm});
        }
        {
            var Q0;
            Q0=makeQuery(id+"F29.opExtrude","CAP_FACE",FACE,{"disambiguationData":[OSD([sQuery(id+"F28.wireOp",EDGE,"E31.bottom"),sQuery(id+"F28.wireOp",EDGE,"E31.top"),sQuery(id+"F28.wireOp",EDGE,"E31.left"),sQuery(id+"F28.wireOp",EDGE,"E31.right")])],"isStart":false});
            var sketch = newSketch(context, id + "F41", { "sketchPlane" : qUnion([Q0])});
            skLineSegment(sketch, "E46.bottom", {"start": v(0, 0) * mm, "end": v(9.52, 0) * mm});
            skLineSegment(sketch, "E46.top", {"start": v(0, 9.52) * mm, "end": v(9.52, 9.52) * mm});
            skLineSegment(sketch, "E46.left", {"start": v(0, 0) * mm, "end": v(0, 9.52) * mm});
            skLineSegment(sketch, "E46.right", {"start": v(9.52, 0) * mm, "end": v(9.52, 9.52) * mm});
            skLineSegment(sketch, "E47.bottom", {"start": v(9.52, 9.52) * mm, "end": v(22.22, 9.52) * mm});
            skLineSegment(sketch, "E47.top", {"start": v(9.52, 22.22) * mm, "end": v(22.22, 22.22) * mm});
            skLineSegment(sketch, "E47.left", {"start": v(9.52, 9.52) * mm, "end": v(9.52, 22.22) * mm});
            skLineSegment(sketch, "E47.right", {"start": v(22.22, 9.52) * mm, "end": v(22.22, 22.22) * mm});
            skSolve(sketch);
        }
        {
            var Q0;
            Q0=makeQuery(id+"F41.imprint","IMPRINT",FACE,{"disambiguationData":[TD([[makeQuery(id+"F41.imprint","IMPRINT",EDGE,{"derivedFrom":sQuery(id+"F41.wireOp",EDGE,"E47.bottom")}),1.0]])]});
            extrude(context, id + "F42", {"entities" : qUnion([Q0]), "operationType" : NewBodyOperationType.REMOVE, "oppositeDirection" : true, "depth" : 736.6 * mm});
        }
        {
            var Q0;
            {var subQ0=sQuery(id+"F30.wireOp",EDGE,"E32.right");var subQ1=sQuery(id+"F30.wireOp",EDGE,"E32.top");var subQ2=makeQuery(id+"F30.imprint","INTERSECT",VERTEX,{"derivedFrom":[subQ1,subQ0]});Q0=makeQuery(id+"F30.imprint","IMPRINT",FACE,{"disambiguationData":[TD([[makeQuery(id+"F30.imprint","IMPRINT",EDGE,{"disambiguationData":[TD([[subQ2,1.0]])],"derivedFrom":subQ1}),-1.0]])]});}
            var Q1;
            {var subQ0=sQuery(id+"F30.wireOp",EDGE,"E32.right");var subQ1=sQuery(id+"F30.wireOp",EDGE,"E32.top");var subQ2=makeQuery(id+"F30.imprint","INTERSECT",VERTEX,{"derivedFrom":[subQ1,subQ0]});Q1=makeQuery(id+"F30.imprint","IMPRINT",FACE,{"disambiguationData":[TD([[makeQuery(id+"F30.imprint","IMPRINT",EDGE,{"disambiguationData":[TD([[subQ2,1.0]])],"derivedFrom":subQ1}),1.0]])]});}
            extrude(context, id + "F43", {"entities" : qUnion([Q0, Q1]), "operationType" : NewBodyOperationType.REMOVE, "oppositeDirection" : true, "depth" : 6.35 * mm});
        }
        {
            var Q0;
            Q0=makeQuery(id+"F1.opExtrude","SWEPT_FACE",FACE,{"disambiguationData":[OSD([sQuery(id+"F0.wireOp",EDGE,"E3")])]});
            var sketch = newSketch(context, id + "F44", { "sketchPlane" : qUnion([Q0])});
            skLineSegment(sketch, "E48.bottom", {"start": v(0, 0) * mm, "end": v(31.75, 0) * mm});
            skLineSegment(sketch, "E48.top", {"start": v(0, 361) * mm, "end": v(31.75, 361) * mm});
            skLineSegment(sketch, "E48.left", {"start": v(0, 0) * mm, "end": v(0, 361) * mm});
            skLineSegment(sketch, "E48.right", {"start": v(31.75, 0) * mm, "end": v(31.75, 361) * mm});
            skSolve(sketch);
        }
        {
            var Q0;
            Q0 = qSketchRegion(id + "F44", true);
            extrude(context, id + "F45", {"entities" : qUnion([Q0]), "operationType" : NewBodyOperationType.REMOVE, "oppositeDirection" : true, "depth" : 76.2 * mm});
        }
        {
            var Q0;
            Q0=makeQuery(id+"F45.boolean.opBoolean","COPY",FACE,{"derivedFrom":makeQuery(id+"F45.opExtrude","SWEPT_FACE",FACE,{"disambiguationData":[OSD([sQuery(id+"F44.wireOp",EDGE,"E48.top")])]})});
            var sketch = newSketch(context, id + "F46", { "sketchPlane" : qUnion([Q0])});
            skLineSegment(sketch, "E49.bottom", {"start": v(0, 0) * mm, "end": v(31.75, 0) * mm});
            skLineSegment(sketch, "E49.top", {"start": v(0, -31.75) * mm, "end": v(31.75, -31.75) * mm});
            skLineSegment(sketch, "E49.left", {"start": v(0, 0) * mm, "end": v(0, -31.75) * mm});
            skLineSegment(sketch, "E49.right", {"start": v(31.75, 0) * mm, "end": v(31.75, -31.75) * mm});
            skLineSegment(sketch, "E50.bottom", {"start": v(3.17, -3.18) * mm, "end": v(28.57, -3.18) * mm});
            skLineSegment(sketch, "E50.top", {"start": v(3.17, -28.58) * mm, "end": v(28.57, -28.58) * mm});
            skLineSegment(sketch, "E50.left", {"start": v(3.17, -3.18) * mm, "end": v(3.17, -28.58) * mm});
            skLineSegment(sketch, "E50.right", {"start": v(28.57, -3.18) * mm, "end": v(28.57, -28.58) * mm});
            skSolve(sketch);
        }
        {
            var Q0;
            Q0=makeQuery(id+"F46.imprint","IMPRINT",FACE,{"disambiguationData":[TD([[makeQuery(id+"F46.imprint","IMPRINT",EDGE,{"derivedFrom":sQuery(id+"F46.wireOp",EDGE,"E50.top")}),1.0]])]});
            var Q1;
            {var subQ0=makeQuery(id+"F45.opExtrude","SWEPT_FACE",FACE,{"disambiguationData":[OSD([sQuery(id+"F44.wireOp",EDGE,"E48.top")])]});Q1=makeQuery(id+"F46.imprint","IMPRINT",FACE,{"disambiguationData":[TD([[makeQuery(id+"F46.imprint","IMPRINT",EDGE,{"derivedFrom":makeQuery(id+"F45.boolean.opBoolean","INTERSECT",EDGE,{"derivedFrom":[makeQuery(id+"F42.boolean.opBoolean","COPY",FACE,{"derivedFrom":makeQuery(id+"F42.opExtrude","SWEPT_FACE",FACE,{"disambiguationData":[OSD([sQuery(id+"F41.wireOp",EDGE,"E47.top")])]})}),subQ0]})}),1.0]])]});}
            extrude(context, id + "F47", {"entities" : qUnion([Q0, Q1]), "operationType" : NewBodyOperationType.REMOVE, "oppositeDirection" : true, "depth" : 12.7 * mm});
        }
    });
